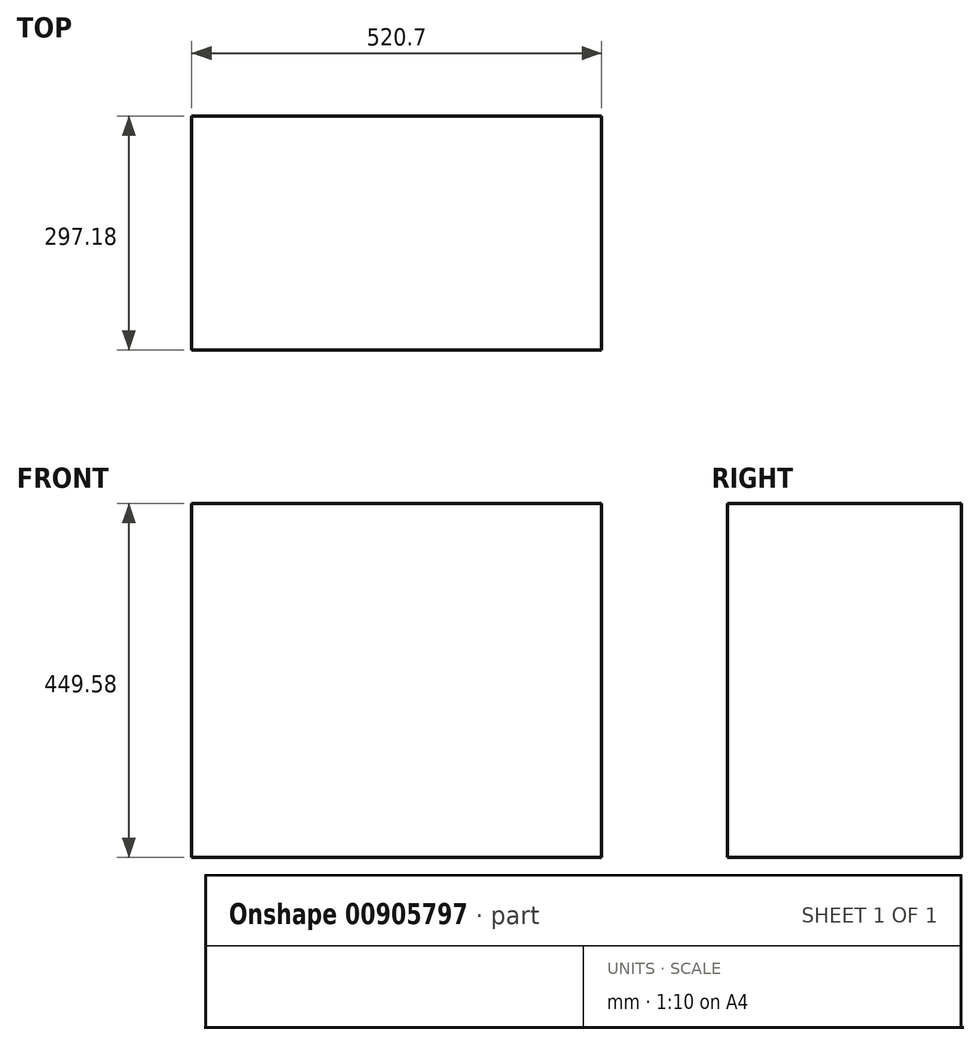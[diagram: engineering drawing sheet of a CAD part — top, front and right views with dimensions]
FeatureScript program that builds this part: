
annotation { "Feature Type Name" : "Feature", "Feature Type Description" : "" }
export const myFeature = defineFeature(function(context is Context, id is Id, definition is map)
    precondition{}
    {
        {
            var Q0;
            Q0=qCreatedBy(makeId("Top.planeOp"),FACE);
            var sketch = newSketch(context, id + "F0", { "sketchPlane" : qUnion([Q0])});
            skLineSegment(sketch, "E0.bottom", {"start": v(-260.35, -148.59) * mm, "end": v(260.35, -148.6) * mm});
            skLineSegment(sketch, "E0.top", {"start": v(-260.35, 148.6) * mm, "end": v(260.35, 148.59) * mm});
            skLineSegment(sketch, "E0.left", {"start": v(-260.35, -148.59) * mm, "end": v(-260.35, 148.59) * mm});
            skLineSegment(sketch, "E0.right", {"start": v(260.35, -148.59) * mm, "end": v(260.35, 148.59) * mm});
            skSolve(sketch);
        }
        {
            var Q0;
            Q0=makeQuery(id+"F0.imprint","IMPRINT",FACE,{"disambiguationData":[TD([[makeQuery(id+"F0.imprint","IMPRINT",EDGE,{"derivedFrom":sQuery(id+"F0.wireOp",EDGE,"E0.bottom")}),1.0]])]});
            extrude(context, id + "F1", {"entities" : qUnion([Q0]), "depth" : 449.58 * mm, "offsetDistance" : 25.4 * mm});
        }
    });
